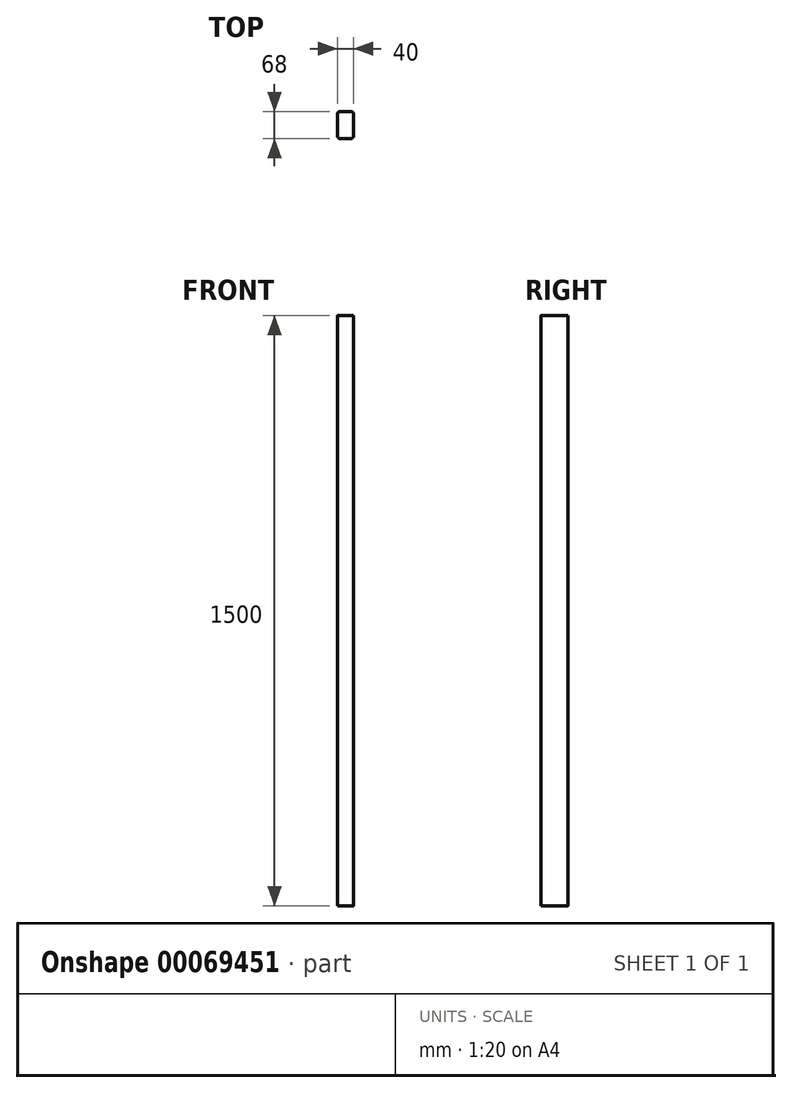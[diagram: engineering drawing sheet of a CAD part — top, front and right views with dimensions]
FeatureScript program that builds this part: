
annotation { "Feature Type Name" : "Feature", "Feature Type Description" : "" }
export const myFeature = defineFeature(function(context is Context, id is Id, definition is map)
    precondition{}
    {
        {
            var Q0;
            Q0=qCreatedBy(makeId("Top.planeOp"),FACE);
            var sketch = newSketch(context, id + "F0", { "sketchPlane" : qUnion([Q0])});
            skLineSegment(sketch, "E0.rect.bottom", {"start": v(15, -34) * mm, "end": v(-15, -34) * mm});
            skLineSegment(sketch, "E0.rect.top", {"start": v(15, 34) * mm, "end": v(-15, 34) * mm});
            skLineSegment(sketch, "E0.rect.left", {"start": v(20, -29) * mm, "end": v(20, 29) * mm});
            skLineSegment(sketch, "E0.rect.right", {"start": v(-20, -29) * mm, "end": v(-20, 29) * mm});
            skPoint(sketch, "E0.rect.middle", {"position": v(0, 0) * mm});
            skPoint(sketch, "E1.visualSharp", {"position": v(-20, -34) * mm});
            skArc(sketch, "E1.filletArc", {"start": v(-20, -29) * mm, "mid": v(-18.54, -32.54) * mm, "end": v(-15, -34) * mm});
            skPoint(sketch, "E2.visualSharp", {"position": v(20, -34) * mm});
            skArc(sketch, "E2.filletArc", {"start": v(15, -34) * mm, "mid": v(18.54, -32.54) * mm, "end": v(20, -29) * mm});
            skPoint(sketch, "E3.visualSharp", {"position": v(20, 34) * mm});
            skArc(sketch, "E3.filletArc", {"start": v(20, 29) * mm, "mid": v(18.54, 32.54) * mm, "end": v(15, 34) * mm});
            skPoint(sketch, "E4.visualSharp", {"position": v(-20, 34) * mm});
            skArc(sketch, "E4.filletArc", {"start": v(-15, 34) * mm, "mid": v(-18.54, 32.54) * mm, "end": v(-20, 29) * mm});
            skSolve(sketch);
        }
        {
            var Q0;
            Q0=makeQuery(id+"F0.imprint","IMPRINT",FACE,{"disambiguationData":[TD([[makeQuery(id+"F0.imprint","IMPRINT",EDGE,{"derivedFrom":sQuery(id+"F0.wireOp",EDGE,"E0.rect.bottom")}),-1.0]])]});
            extrude(context, id + "F1", {"entities" : qUnion([Q0]), "depth" : 1500 * mm});
        }
    });
